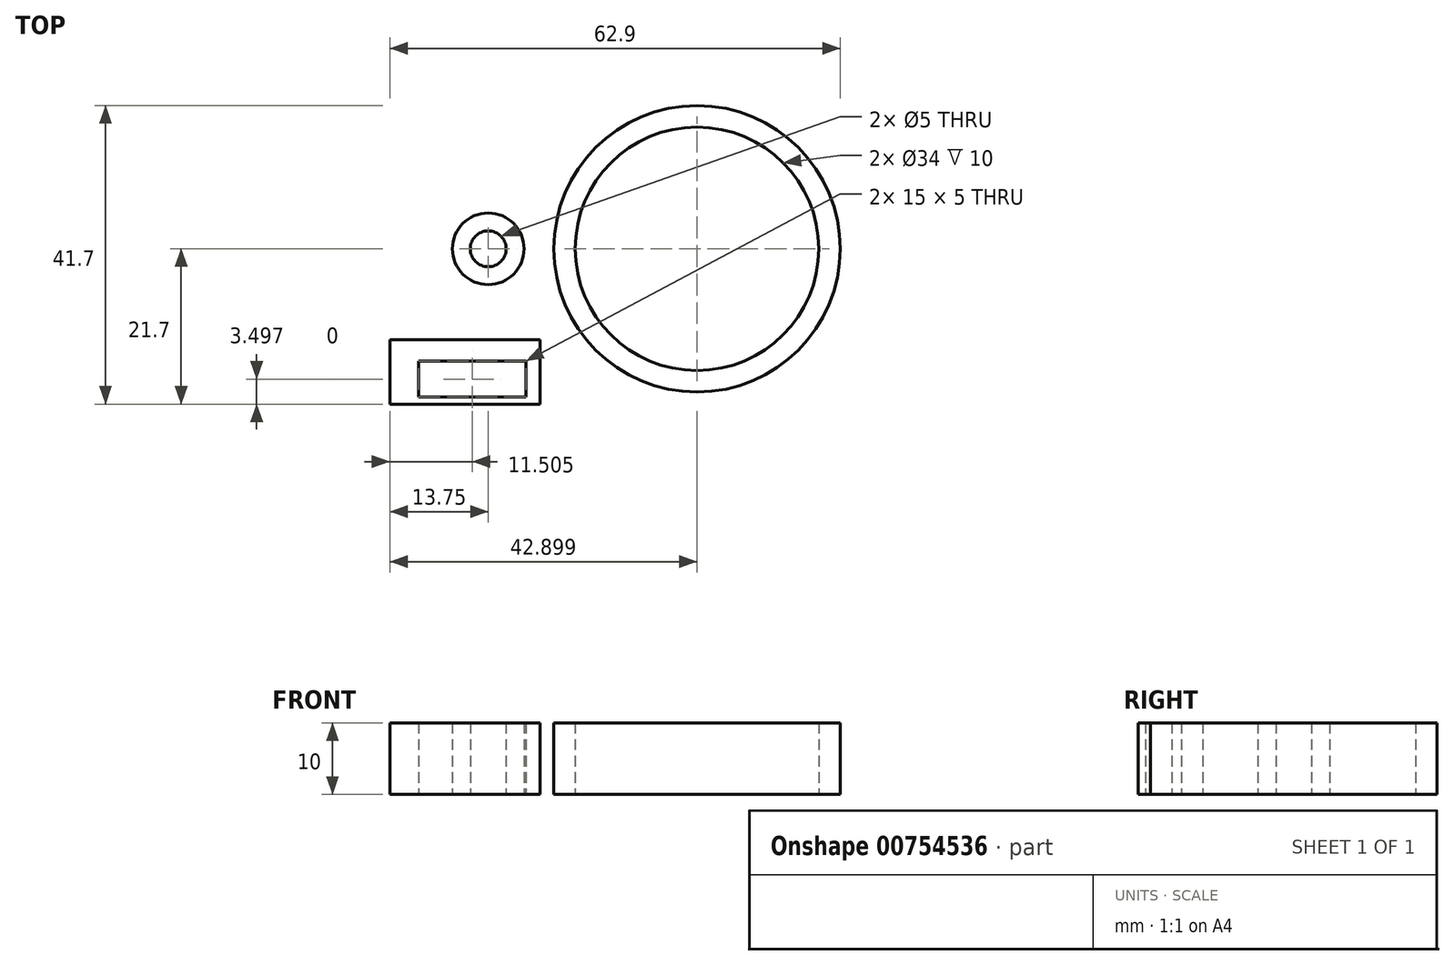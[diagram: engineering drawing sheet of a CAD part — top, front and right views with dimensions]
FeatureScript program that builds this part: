
annotation { "Feature Type Name" : "Feature", "Feature Type Description" : "" }
export const myFeature = defineFeature(function(context is Context, id is Id, definition is map)
    precondition{}
    {
        {
            var Q0;
            Q0=qCreatedBy(makeId("Top.planeOp"),FACE);
            var sketch = newSketch(context, id + "F0", { "sketchPlane" : qUnion([Q0])});
            skCircle(sketch, "E0", {"center": v(0, 0) * mm, "radius": 5 * mm});
            skCircle(sketch, "E1", {"center": v(29.15, 0) * mm, "radius": 20 * mm});
            skCircle(sketch, "E2", {"center": v(29.15, 0) * mm, "radius": 17 * mm});
            skLineSegment(sketch, "E3", {"start": v(0, 0) * mm, "end": v(29.15, 0) * mm, "construction": true});
            skCircle(sketch, "E4", {"center": v(0, 0) * mm, "radius": 2.5 * mm});
            skSolve(sketch);
        }
        {
            var Q0;
            Q0=makeQuery(id+"F0.imprint","IMPRINT",FACE,{"disambiguationData":[TD([[makeQuery(id+"F0.imprint","IMPRINT",EDGE,{"derivedFrom":sQuery(id+"F0.wireOp",EDGE,"E1")}),1.0]])]});
            var Q1;
            Q1=makeQuery(id+"F0.imprint","IMPRINT",FACE,{"disambiguationData":[TD([[makeQuery(id+"F0.imprint","IMPRINT",EDGE,{"derivedFrom":sQuery(id+"F0.wireOp",EDGE,"E0")}),1.0]])]});
            extrude(context, id + "F1", {"entities" : qUnion([Q0, Q1]), "depth" : 10 * mm, "offsetDistance" : 25.4 * mm});
        }
        {
            var Q0;
            Q0=qCreatedBy(makeId("Top.planeOp"),FACE);
            var sketch = newSketch(context, id + "F2", { "sketchPlane" : qUnion([Q0])});
            skLineSegment(sketch, "E5.bottom", {"start": v(-9.75, -20.7) * mm, "end": v(5.25, -20.7) * mm});
            skLineSegment(sketch, "E5.top", {"start": v(-9.75, -15.7) * mm, "end": v(5.25, -15.7) * mm});
            skLineSegment(sketch, "E5.left", {"start": v(-9.75, -20.7) * mm, "end": v(-9.75, -15.7) * mm});
            skLineSegment(sketch, "E5.right", {"start": v(5.25, -20.7) * mm, "end": v(5.25, -15.7) * mm});
            skLineSegment(sketch, "E6.bottom", {"start": v(-13.75, -12.7) * mm, "end": v(7.25, -12.7) * mm});
            skLineSegment(sketch, "E6.top", {"start": v(-13.75, -21.7) * mm, "end": v(7.25, -21.7) * mm});
            skLineSegment(sketch, "E6.left", {"start": v(-13.75, -12.7) * mm, "end": v(-13.75, -21.7) * mm});
            skLineSegment(sketch, "E6.right", {"start": v(7.25, -12.7) * mm, "end": v(7.25, -21.7) * mm});
            skSolve(sketch);
        }
        {
            var Q0;
            Q0=makeQuery(id+"F2.imprint","IMPRINT",FACE,{"disambiguationData":[TD([[makeQuery(id+"F2.imprint","IMPRINT",EDGE,{"derivedFrom":sQuery(id+"F2.wireOp",EDGE,"E5.bottom")}),-1.0]])]});
            extrude(context, id + "F3", {"entities" : qUnion([Q0]), "depth" : 10 * mm, "offsetDistance" : 25.4 * mm});
        }
    });
